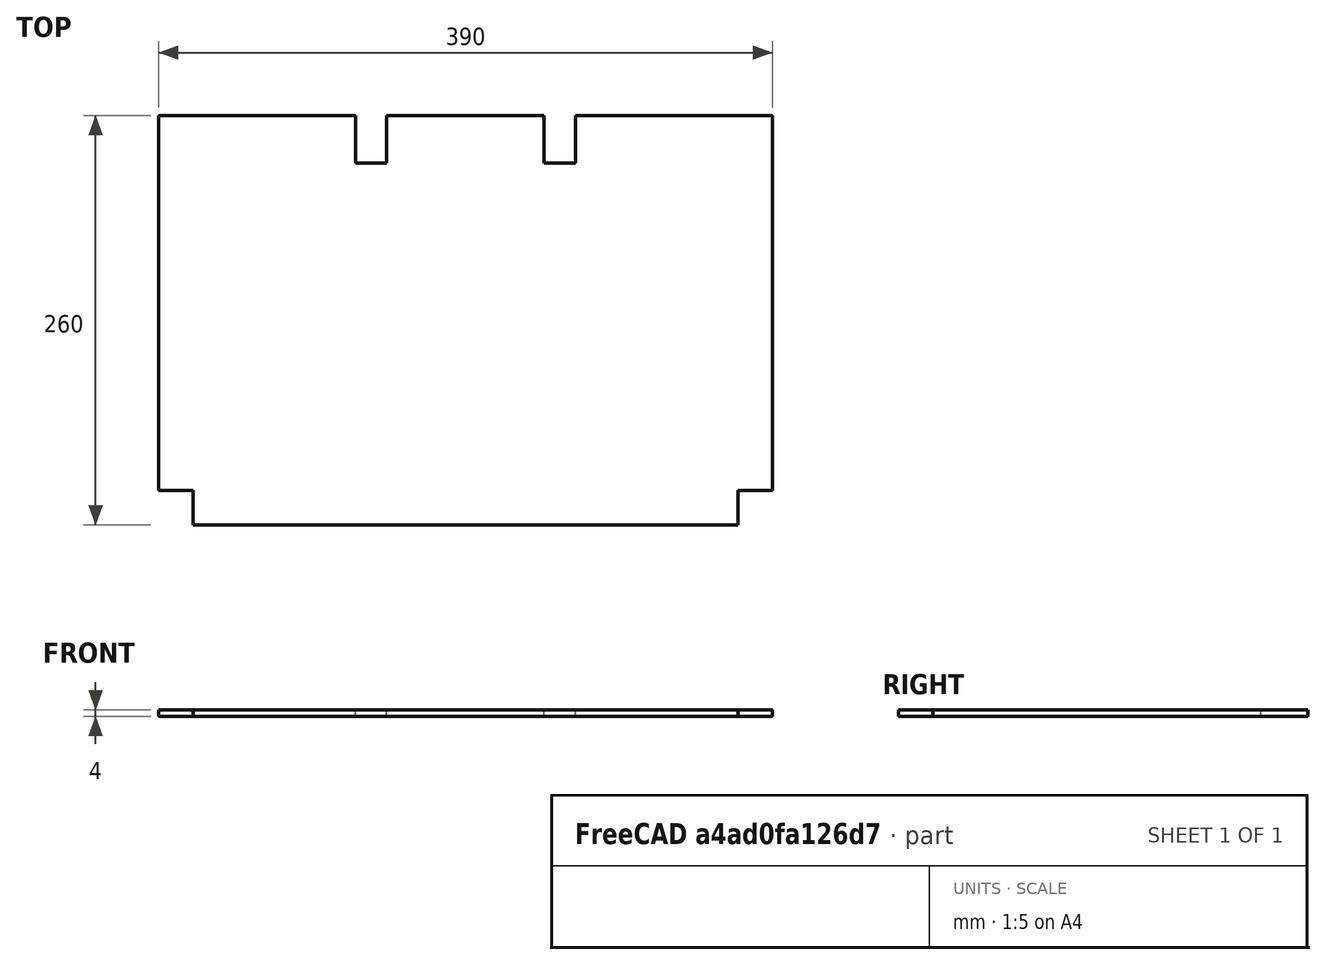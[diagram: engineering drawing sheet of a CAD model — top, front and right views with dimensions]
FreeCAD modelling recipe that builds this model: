
FCSTD DOCUMENT  (FreeCAD 0.14R3703 (Git))
Label: soporte_cubeta
License: CC-BY 3.0
LicenseURL: http://creativecommons.org/licenses/by/3.0/
objects: Part::Box×5, Part::Cut×4, App::DocumentObjectGroup×1
note: 9 computed .brp shape members not serialized (recipe doc carries the construction recipe); baked Part::Feature solids carry a one-line shape summary decoded from their .brp

FEATURE [Part::Box] Box  label="plancha_aluminio"
  Height = 4
  Length = 390
  Width = 260
FEATURE [Part::Box] Box001  label="corte_izq"
  Height = 10
  Length = 22
  Placement = pos=(0,0,-3) rot=(0,0,1;0rad)
  Width = 22
FEATURE [Part::Box] Box002  label="corte_der"
  Height = 10
  Length = 22
  Placement = pos=(368,0,-3) rot=(0,0,1;0rad)
  Width = 22
FEATURE [Part::Cut] Cut
  Base = -> Box
  Tool = -> Box001
FEATURE [Part::Cut] Cut001
  Base = -> Cut
  Tool = -> Box002
FEATURE [Part::Box] Box003  label="corte_rail_izq"
  Height = 10
  Length = 20
  Placement = pos=(125,230,-3) rot=(0,0,1;0rad)
  Width = 30
FEATURE [Part::Box] Box004  label="corte_rail_der"
  Height = 10
  Length = 20
  Placement = pos=(245,230,-3) rot=(0,0,1;0rad)
  Width = 30
FEATURE [Part::Cut] Cut002
  Base = -> Cut001
  Tool = -> Box003
FEATURE [Part::Cut] Cut003  label="soporte_cubeta"
  Base = -> Cut002
  Tool = -> Box004
FEATURE [App::DocumentObjectGroup] Grupo  label="soporte_cubeta001"
  Group = -> [Cut003]
